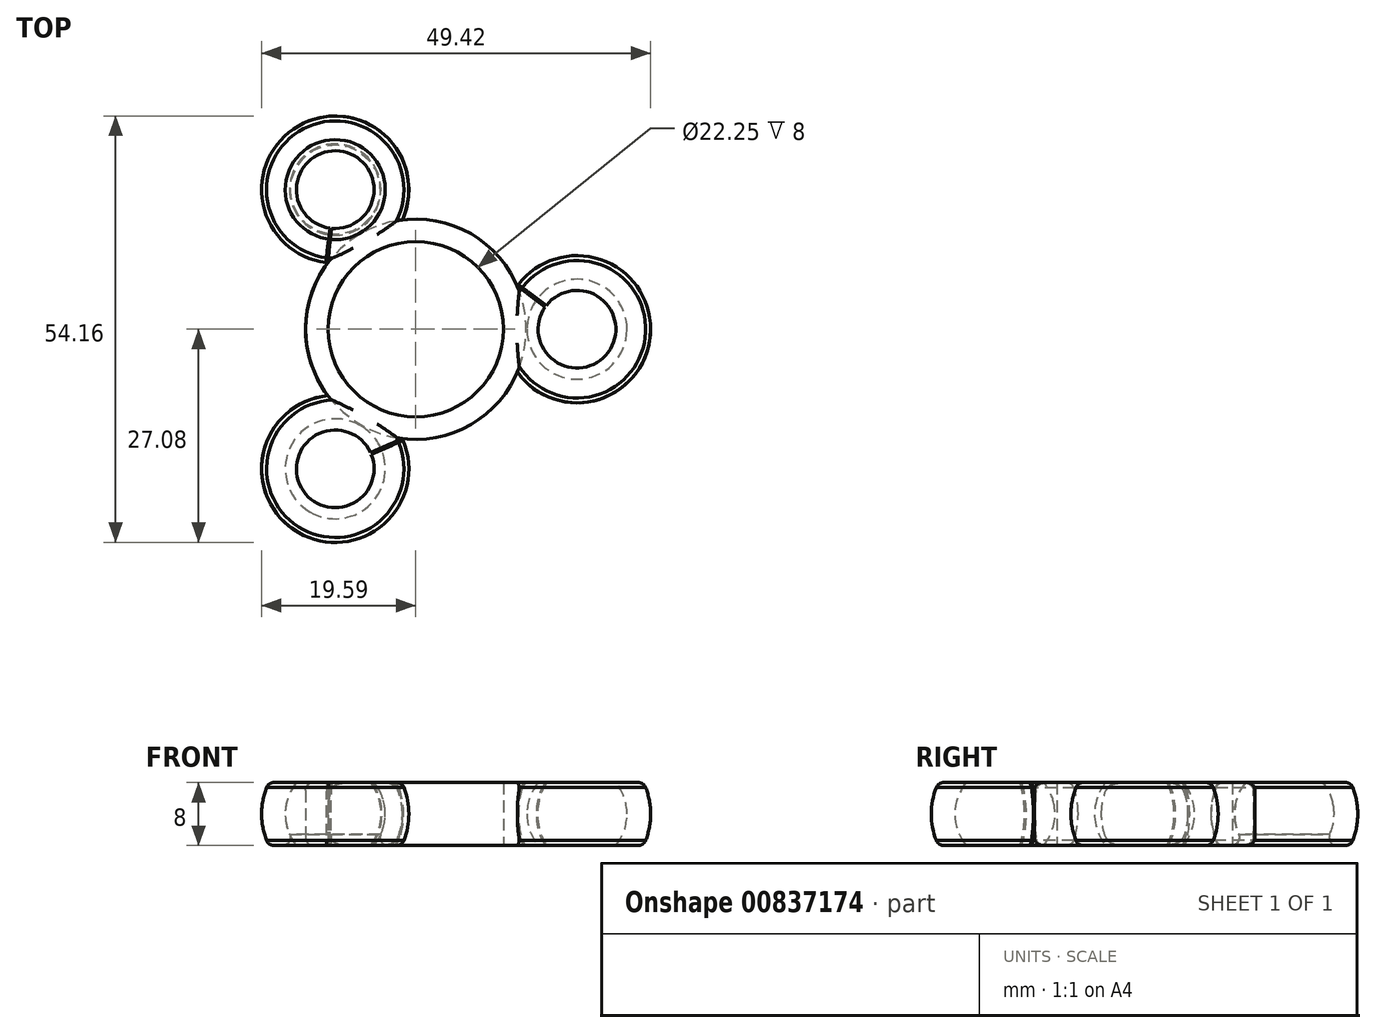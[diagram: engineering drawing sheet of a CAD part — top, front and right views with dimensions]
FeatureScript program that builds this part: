
annotation { "Feature Type Name" : "Feature", "Feature Type Description" : "" }
export const myFeature = defineFeature(function(context is Context, id is Id, definition is map)
    precondition{}
    {
        {
            var Q0;
            Q0=qCreatedBy(makeId("Top.planeOp"),FACE);
            var sketch = newSketch(context, id + "F0", { "sketchPlane" : qUnion([Q0])});
            skArc(sketch, "E0", {"start": v(29.82, 0) * mm, "mid": v(20.48, 9.35) * mm, "end": v(11.12, 0) * mm});
            skArc(sketch, "E1", {"start": v(26.83, 0) * mm, "mid": v(20.48, 6.35) * mm, "end": v(14.12, 0) * mm});
            skPoint(sketch, "E2.center", {"position": v(0, 0) * mm});
            skPoint(sketch, "E3", {"position": v(11.12, 0) * mm});
            skLineSegment(sketch, "E4", {"start": v(20.48, 0) * mm, "end": v(12.96, 5.57) * mm, "construction": true});
            skLineSegment(sketch, "E5", {"start": v(12.89, 5.47) * mm, "end": v(20.27, 0) * mm});
            skLineSegment(sketch, "E6", {"start": v(13.04, 5.67) * mm, "end": v(20.68, 0) * mm});
            skLineSegment(sketch, "E7", {"start": v(16.58, 2.73) * mm, "end": v(16.73, 2.93) * mm, "construction": true});
            skPoint(sketch, "E8", {"position": v(16.65, 2.83) * mm});
            skLineSegment(sketch, "E9", {"start": v(11.12, 0) * mm, "end": v(29.82, 0) * mm});
            skCircle(sketch, "E10.converted", {"center": v(0, 0) * mm, "radius": 14 * mm});
            skCircle(sketch, "E11.converted", {"center": v(0, 0) * mm, "radius": 11.12 * mm});
            skSolve(sketch);
        }
        {
            var Q0;
            {var subQ0=sQuery(id+"F0.wireOp",EDGE,"E9");var subQ1=sQuery(id+"F0.wireOp",EDGE,"E0");var subQ2=makeQuery(id+"F0.imprint","INTERSECT",VERTEX,{"derivedFrom":[subQ1,subQ0]});Q0=makeQuery(id+"F0.imprint","IMPRINT",FACE,{"disambiguationData":[TD([[makeQuery(id+"F0.imprint","IMPRINT",EDGE,{"disambiguationData":[TD([[subQ2,-1.0]])],"derivedFrom":subQ1}),1.0]])]});}
            var Q1;
            {var subQ0=sQuery(id+"F0.wireOp",EDGE,"E9");var subQ1=sQuery(id+"F0.wireOp",EDGE,"E0");var subQ2=makeQuery(id+"F0.imprint","INTERSECT",VERTEX,{"derivedFrom":[sQuery(id+"F0.wireOp",EDGE,"cSuj2Qlp-0pDQ-TG8P-6tV9-5ENMxgLf1ts3"),subQ1,subQ0]});Q1=makeQuery(id+"F0.imprint","IMPRINT",FACE,{"disambiguationData":[TD([[makeQuery(id+"F0.imprint","IMPRINT",EDGE,{"disambiguationData":[TD([[subQ2,1.0]])],"derivedFrom":subQ1}),1.0]])]});}
            var Q2;
            {var subQ1=sQuery(id+"F0.wireOp",EDGE,"E1");var subQ3=sQuery(id+"F0.wireOp",EDGE,"E5");var subQ4=makeQuery(id+"F0.imprint","INTERSECT",VERTEX,{"derivedFrom":[subQ1,subQ3]});Q2=makeQuery(id+"F0.imprint","IMPRINT",FACE,{"disambiguationData":[TD([[makeQuery(id+"F0.imprint","IMPRINT",EDGE,{"disambiguationData":[TD([[subQ4,-1.0]])],"derivedFrom":subQ1}),-1.0]])]});}
            var Q3;
            {var subQ3=sQuery(id+"F0.wireOp",EDGE,"E6");var subQ5=sQuery(id+"F0.wireOp",EDGE,"E1");var subQ7=makeQuery(id+"F0.imprint","INTERSECT",VERTEX,{"derivedFrom":[subQ5,subQ3]});Q3=makeQuery(id+"F0.imprint","IMPRINT",FACE,{"disambiguationData":[TD([[makeQuery(id+"F0.imprint","IMPRINT",EDGE,{"disambiguationData":[TD([[subQ7,-1.0]])],"derivedFrom":subQ5}),-1.0]])]});}
            var Q4;
            {var subQ0=sQuery(id+"F0.wireOp",EDGE,"E9");var subQ3=sQuery(id+"F0.wireOp",EDGE,"E10.converted");var subQ5=makeQuery(id+"F0.imprint","INTERSECT",VERTEX,{"derivedFrom":[subQ0,subQ3]});Q4=makeQuery(id+"F0.imprint","IMPRINT",FACE,{"disambiguationData":[TD([[makeQuery(id+"F0.imprint","IMPRINT",EDGE,{"disambiguationData":[TD([[subQ5,1.0]])],"derivedFrom":subQ0}),1.0]])]});}
            var Q5;
            Q5=sQuery(id+"F0.wireOp",EDGE,"E9");
            revolve(context, id + "F1", {"surfaceOperationType" : NewSurfaceOperationType.NEW, "entities" : qUnion([Q0, Q1, Q2, Q3, Q4]), "axis" : qUnion([Q5]), "revolveType" : RevolveType.FULL});
        }
        {
            var Q0;
            {var subQ0=sQuery(id+"F0.wireOp",EDGE,"E11.converted");Q0=makeQuery(id+"F0.imprint","IMPRINT",FACE,{"disambiguationData":[TD([[makeQuery(id+"F0.imprint","IMPRINT",EDGE,{"derivedFrom":subQ0}),-1.0]])]});}
            var Q1;
            {var subQ0=sQuery(id+"F0.wireOp",EDGE,"E9");var subQ3=sQuery(id+"F0.wireOp",EDGE,"E10.converted");var subQ5=makeQuery(id+"F0.imprint","INTERSECT",VERTEX,{"derivedFrom":[subQ0,subQ3]});Q1=makeQuery(id+"F0.imprint","IMPRINT",FACE,{"disambiguationData":[TD([[makeQuery(id+"F0.imprint","IMPRINT",EDGE,{"disambiguationData":[TD([[subQ5,1.0]])],"derivedFrom":subQ0}),1.0]])]});}
            extrude(context, id + "F2", {"entities" : qUnion([Q0, Q1]), "endBound" : BoundingType.SYMMETRIC, "depth" : 8 * mm, "offsetDistance" : 25 * mm});
        }
        {
            var Q0;
            {var subQ3=sQuery(id+"F0.wireOp",EDGE,"E6");var subQ5=sQuery(id+"F0.wireOp",EDGE,"E1");var subQ7=makeQuery(id+"F0.imprint","INTERSECT",VERTEX,{"derivedFrom":[subQ5,subQ3]});Q0=makeQuery(id+"F0.imprint","IMPRINT",FACE,{"disambiguationData":[TD([[makeQuery(id+"F0.imprint","IMPRINT",EDGE,{"disambiguationData":[TD([[subQ7,-1.0]])],"derivedFrom":subQ5}),-1.0]])]});}
            var Q1;
            {var subQ0=sQuery(id+"F0.wireOp",EDGE,"E6");var subQ1=sQuery(id+"F0.wireOp",EDGE,"E1");var subQ2=makeQuery(id+"F0.imprint","INTERSECT",VERTEX,{"derivedFrom":[subQ1,subQ0]});Q1=makeQuery(id+"F0.imprint","IMPRINT",FACE,{"disambiguationData":[TD([[makeQuery(id+"F0.imprint","IMPRINT",EDGE,{"disambiguationData":[TD([[subQ2,-1.0]])],"derivedFrom":subQ1}),1.0]])]});}
            extrude(context, id + "F3", {"entities" : qUnion([Q0, Q1]), "operationType" : NewBodyOperationType.REMOVE, "endBound" : BoundingType.SYMMETRIC, "oppositeDirection" : true, "depth" : 25 * mm, "offsetDistance" : 25 * mm});
        }
        {
            var Q0;
            Q0=makeQuery(id+"F2.opExtrude","CAP_FACE",FACE,{"disambiguationData":[OSD([sQuery(id+"F0.wireOp",EDGE,"E10.converted"),sQuery(id+"F0.wireOp",EDGE,"E11.converted")])],"isStart":false});
            var sketch = newSketch(context, id + "F4", { "sketchPlane" : qUnion([Q0])});
            skCircle(sketch, "E12", {"center": v(20.48, 0) * mm, "radius": 9.35 * mm});
            skSolve(sketch);
        }
        {
            var Q0;
            {var subQ0=sQuery(id+"F4.wireOp",EDGE,"E12");var subQ1=makeQuery(id+"F2.opExtrude","CAP_EDGE",EDGE,{"disambiguationData":[OSD([sQuery(id+"F0.wireOp",EDGE,"EpLUkTgh-srj3-UDcm-vpLL-Aj0M4960BcQC")])],"isStart":false});var subQ2=makeQuery(id+"F4.imprint","INTERSECT",VERTEX,{"disambiguationData":[OD(0.0)],"derivedFrom":[subQ1,subQ0]});Q0=makeQuery(id+"F4.imprint","IMPRINT",FACE,{"disambiguationData":[TD([[makeQuery(id+"F4.imprint","IMPRINT",EDGE,{"disambiguationData":[TD([[subQ2,1.0]])],"derivedFrom":subQ0}),1.0]])]});}
            var Q1;
            {var subQ0=sQuery(id+"F4.wireOp",EDGE,"E12");var subQ1=makeQuery(id+"F4.imprint","INTERSECT",VERTEX,{"derivedFrom":[makeQuery(id+"F2.opExtrude","CAP_EDGE",EDGE,{"disambiguationData":[OSD([sQuery(id+"F0.wireOp",EDGE,"cSuj2Qlp-0pDQ-TG8P-6tV9-5ENMxgLf1ts3")])],"isStart":false}),subQ0]});Q1=makeQuery(id+"F4.imprint","IMPRINT",FACE,{"disambiguationData":[TD([[makeQuery(id+"F4.imprint","IMPRINT",EDGE,{"disambiguationData":[TD([[subQ1,1.0]])],"derivedFrom":subQ0}),1.0]])]});}
            extrude(context, id + "F5", {"entities" : qUnion([Q0, Q1]), "endBound" : BoundingType.THROUGH_ALL, "depth" : 25 * mm, "offsetDistance" : 25 * mm});
        }
        {
            var Q0;
            Q0=makeQuery(id+"F5.opExtrude","SWEPT_BODY",BODY,{"disambiguationData":[OSD([sQuery(id+"F4.wireOp",EDGE,"E12")])]});
            var Q1;
            Q1=qCreatedBy(makeId("Top.planeOp"),FACE);
            mirror(context, id + "F6", {"entities" : qUnion([Q0]), "mirrorPlane" : qUnion([Q1])});
        }
        {
            var Q0;
            Q0=makeQuery(id+"F5.opExtrude","SWEPT_BODY",BODY,{"disambiguationData":[OSD([sQuery(id+"F4.wireOp",EDGE,"E12")])]});
            var Q1;
            Q1=makeQuery(id+"F6.opPattern","COPY",BODY,{"derivedFrom":makeQuery(id+"F5.opExtrude","SWEPT_BODY",BODY,{"disambiguationData":[OSD([sQuery(id+"F4.wireOp",EDGE,"E12")])]}),"instanceName":"1"});
            var Q2;
            Q2=makeQuery(id+"F2.opExtrude","SWEPT_BODY",BODY,{"disambiguationData":[OSD([sQuery(id+"F0.wireOp",EDGE,"cSuj2Qlp-0pDQ-TG8P-6tV9-5ENMxgLf1ts3"),sQuery(id+"F0.wireOp",EDGE,"EpLUkTgh-srj3-UDcm-vpLL-Aj0M4960BcQC"),sQuery(id+"F0.wireOp",EDGE,"zkzayk11-GNPU-wToI-XGPR-Ek0oZkHYU3Nr"),sQuery(id+"F0.wireOp",EDGE,"hWNBNIeG-xdyR-n3hM-UmGh-ZOXQKCDM2jcM")])]});
            var Q3;
            Q3=makeQuery(id+"F1.opRevolve","SWEPT_BODY",BODY,{"disambiguationData":[OSD([sQuery(id+"F0.wireOp",EDGE,"E0"),sQuery(id+"F0.wireOp",EDGE,"E1"),sQuery(id+"F0.wireOp",EDGE,"E9")])]});
            booleanBodies(context, id + "F7", {"operationType" : BooleanOperationType.SUBTRACTION, "tools" : qUnion([Q0, Q1]), "targets" : qUnion([Q2, Q3])});
        }
        {
            var Q0;
            Q0=qCreatedBy(makeId("Front.planeOp"),FACE);
            var sketch = newSketch(context, id + "F8", { "sketchPlane" : qUnion([Q0])});
            skLineSegment(sketch, "E13", {"start": v(0, 0) * mm, "end": v(0, 13.43) * mm, "construction": true});
            skSolve(sketch);
        }
        {
            var Q0;
            Q0=makeQuery(id+"F1.opRevolve","SWEPT_BODY",BODY,{"disambiguationData":[OSD([sQuery(id+"F0.wireOp",EDGE,"E0"),sQuery(id+"F0.wireOp",EDGE,"E1"),sQuery(id+"F0.wireOp",EDGE,"E9")])]});
            var Q1;
            Q1=sQuery(id+"F8.wireOp",EDGE,"E13");
            circularPattern(context, id + "F9", {"entities" : qUnion([Q0]), "axis" : qUnion([Q1]), "angle" : 360 * degree, "instanceCount" : 3, "equalSpace" : true});
        }
        {
            var Q0;
            Q0=makeQuery(id+"F1.opRevolve","SWEPT_BODY",BODY,{"disambiguationData":[OSD([sQuery(id+"F0.wireOp",EDGE,"E0"),sQuery(id+"F0.wireOp",EDGE,"E1"),sQuery(id+"F0.wireOp",EDGE,"E9")])]});
            var Q1;
            Q1=makeQuery(id+"F2.opExtrude","SWEPT_BODY",BODY,{"disambiguationData":[OSD([sQuery(id+"F0.wireOp",EDGE,"cSuj2Qlp-0pDQ-TG8P-6tV9-5ENMxgLf1ts3"),sQuery(id+"F0.wireOp",EDGE,"EpLUkTgh-srj3-UDcm-vpLL-Aj0M4960BcQC"),sQuery(id+"F0.wireOp",EDGE,"zkzayk11-GNPU-wToI-XGPR-Ek0oZkHYU3Nr"),sQuery(id+"F0.wireOp",EDGE,"hWNBNIeG-xdyR-n3hM-UmGh-ZOXQKCDM2jcM")])]});
            var Q2;
            Q2=makeQuery(id+"F9.opPattern","COPY",BODY,{"derivedFrom":makeQuery(id+"F1.opRevolve","SWEPT_BODY",BODY,{"disambiguationData":[OSD([sQuery(id+"F0.wireOp",EDGE,"E0"),sQuery(id+"F0.wireOp",EDGE,"E1"),sQuery(id+"F0.wireOp",EDGE,"E9")])]}),"instanceName":"1"});
            var Q3;
            Q3=makeQuery(id+"F9.opPattern","COPY",BODY,{"derivedFrom":makeQuery(id+"F1.opRevolve","SWEPT_BODY",BODY,{"disambiguationData":[OSD([sQuery(id+"F0.wireOp",EDGE,"E0"),sQuery(id+"F0.wireOp",EDGE,"E1"),sQuery(id+"F0.wireOp",EDGE,"E9")])]}),"instanceName":"2"});
            var Q4;
            Q4=makeQuery(id+"F2.opExtrude","SWEPT_BODY",BODY,{"disambiguationData":[OSD([sQuery(id+"F0.wireOp",EDGE,"E10.converted"),sQuery(id+"F0.wireOp",EDGE,"E11.converted")])]});
            booleanBodies(context, id + "F10", {"operationType" : BooleanOperationType.UNION, "tools" : qUnion([Q0, Q1, Q2, Q3, Q4])});
        }
        {
            var Q0;
            {var subQ0=makeQuery(id+"F7.opBoolean","COPY",FACE,{"derivedFrom":makeQuery(id+"F5.opExtrude","CAP_FACE",FACE,{"disambiguationData":[OSD([sQuery(id+"F4.wireOp",EDGE,"E12")])],"isStart":true})});var subQ1=sQuery(id+"F0.wireOp",EDGE,"E10.converted");var subQ2=makeQuery(id+"F1.opRevolve","SWEPT_FACE",FACE,{"disambiguationData":[OSD([sQuery(id+"F0.wireOp",EDGE,"E0")])]});Q0=makeQuery(id+"F10.opBoolean","SPLIT",EDGE,{"disambiguationData":[TD([makeQuery(id+"F2.opExtrude","SWEPT_FACE",FACE,{"disambiguationData":[OSD([subQ1])]}),makeQuery(id+"F2.opExtrude","CAP_FACE",FACE,{"disambiguationData":[OSD([subQ1,sQuery(id+"F0.wireOp",EDGE,"E11.converted")])],"isStart":false}),subQ0,makeQuery(id+"F9.opPattern","COPY",FACE,{"derivedFrom":subQ0,"instanceName":"1"}),makeQuery(id+"F9.opPattern","COPY",FACE,{"derivedFrom":subQ2,"instanceName":"1"}),makeQuery(id+"F9.opPattern","COPY",FACE,{"derivedFrom":subQ0,"instanceName":"2"}),makeQuery(id+"F9.opPattern","COPY",FACE,{"derivedFrom":subQ2,"instanceName":"2"})])],"derivedFrom":makeQuery(id+"F2.opExtrude","CAP_EDGE",EDGE,{"disambiguationData":[OSD([subQ1])],"isStart":false})});}
            var Q1;
            {var subQ0=makeQuery(id+"F5.opExtrude","CAP_FACE",FACE,{"disambiguationData":[OSD([sQuery(id+"F4.wireOp",EDGE,"E12")])],"isStart":true});var subQ3=makeQuery(id+"F1.opRevolve","SWEPT_FACE",FACE,{"disambiguationData":[OSD([sQuery(id+"F0.wireOp",EDGE,"E0")])]});Q1=makeQuery(id+"F10.opBoolean","SPLIT",EDGE,{"disambiguationData":[TD([makeQuery(id+"F9.opPattern","COPY",FACE,{"derivedFrom":makeQuery(id+"F3.boolean.opBoolean","COPY",FACE,{"derivedFrom":makeQuery(id+"F3.opExtrude","SWEPT_FACE",FACE,{"disambiguationData":[OSD([sQuery(id+"F0.wireOp",EDGE,"E6")])]})}),"instanceName":"2"})])],"derivedFrom":makeQuery(id+"F9.opPattern","COPY",EDGE,{"derivedFrom":makeQuery(id+"F7.opBoolean","INTERSECT",EDGE,{"derivedFrom":[subQ3,subQ0]}),"instanceName":"2"})});}
            var Q2;
            {var subQ0=makeQuery(id+"F7.opBoolean","COPY",FACE,{"derivedFrom":makeQuery(id+"F5.opExtrude","CAP_FACE",FACE,{"disambiguationData":[OSD([sQuery(id+"F4.wireOp",EDGE,"E12")])],"isStart":true})});var subQ1=sQuery(id+"F0.wireOp",EDGE,"E10.converted");var subQ2=makeQuery(id+"F1.opRevolve","SWEPT_FACE",FACE,{"disambiguationData":[OSD([sQuery(id+"F0.wireOp",EDGE,"E0")])]});Q2=makeQuery(id+"F10.opBoolean","SPLIT",EDGE,{"disambiguationData":[TD([subQ2,makeQuery(id+"F2.opExtrude","SWEPT_FACE",FACE,{"disambiguationData":[OSD([subQ1])]}),makeQuery(id+"F2.opExtrude","CAP_FACE",FACE,{"disambiguationData":[OSD([subQ1,sQuery(id+"F0.wireOp",EDGE,"E11.converted")])],"isStart":false}),subQ0,makeQuery(id+"F9.opPattern","COPY",FACE,{"derivedFrom":subQ0,"instanceName":"1"}),makeQuery(id+"F9.opPattern","COPY",FACE,{"derivedFrom":subQ0,"instanceName":"2"}),makeQuery(id+"F9.opPattern","COPY",FACE,{"derivedFrom":subQ2,"instanceName":"2"})])],"derivedFrom":makeQuery(id+"F2.opExtrude","CAP_EDGE",EDGE,{"disambiguationData":[OSD([subQ1])],"isStart":false})});}
            var Q3;
            {var subQ1=makeQuery(id+"F5.opExtrude","CAP_FACE",FACE,{"disambiguationData":[OSD([sQuery(id+"F4.wireOp",EDGE,"E12")])],"isStart":true});var subQ3=makeQuery(id+"F1.opRevolve","SWEPT_FACE",FACE,{"disambiguationData":[OSD([sQuery(id+"F0.wireOp",EDGE,"E0")])]});Q3=makeQuery(id+"F10.opBoolean","SPLIT",EDGE,{"disambiguationData":[TD([makeQuery(id+"F3.boolean.opBoolean","COPY",FACE,{"derivedFrom":makeQuery(id+"F3.opExtrude","SWEPT_FACE",FACE,{"disambiguationData":[OSD([sQuery(id+"F0.wireOp",EDGE,"E6")])]})})])],"derivedFrom":makeQuery(id+"F7.opBoolean","INTERSECT",EDGE,{"derivedFrom":[subQ3,subQ1]})});}
            var Q4;
            {var subQ0=makeQuery(id+"F5.opExtrude","CAP_FACE",FACE,{"disambiguationData":[OSD([sQuery(id+"F4.wireOp",EDGE,"E12")])],"isStart":true});var subQ3=makeQuery(id+"F1.opRevolve","SWEPT_FACE",FACE,{"disambiguationData":[OSD([sQuery(id+"F0.wireOp",EDGE,"E0")])]});Q4=makeQuery(id+"F10.opBoolean","SPLIT",EDGE,{"disambiguationData":[TD([makeQuery(id+"F9.opPattern","COPY",FACE,{"derivedFrom":makeQuery(id+"F3.boolean.opBoolean","COPY",FACE,{"derivedFrom":makeQuery(id+"F3.opExtrude","SWEPT_FACE",FACE,{"disambiguationData":[OSD([sQuery(id+"F0.wireOp",EDGE,"E6")])]})}),"instanceName":"1"})])],"derivedFrom":makeQuery(id+"F9.opPattern","COPY",EDGE,{"derivedFrom":makeQuery(id+"F7.opBoolean","INTERSECT",EDGE,{"derivedFrom":[subQ3,subQ0]}),"instanceName":"1"})});}
            var Q5;
            {var subQ1=makeQuery(id+"F6.opPattern","COPY",FACE,{"derivedFrom":makeQuery(id+"F5.opExtrude","CAP_FACE",FACE,{"disambiguationData":[OSD([sQuery(id+"F4.wireOp",EDGE,"E12")])],"isStart":true}),"instanceName":"1"});var subQ3=makeQuery(id+"F1.opRevolve","SWEPT_FACE",FACE,{"disambiguationData":[OSD([sQuery(id+"F0.wireOp",EDGE,"E0")])]});Q5=makeQuery(id+"F10.opBoolean","SPLIT",EDGE,{"disambiguationData":[TD([makeQuery(id+"F3.boolean.opBoolean","COPY",FACE,{"derivedFrom":makeQuery(id+"F3.opExtrude","SWEPT_FACE",FACE,{"disambiguationData":[OSD([sQuery(id+"F0.wireOp",EDGE,"E6")])]})})])],"derivedFrom":makeQuery(id+"F7.opBoolean","INTERSECT",EDGE,{"derivedFrom":[subQ3,subQ1]})});}
            var Q6;
            {var subQ0=sQuery(id+"F0.wireOp",EDGE,"E10.converted");var subQ1=makeQuery(id+"F7.opBoolean","COPY",FACE,{"derivedFrom":makeQuery(id+"F6.opPattern","COPY",FACE,{"derivedFrom":makeQuery(id+"F5.opExtrude","CAP_FACE",FACE,{"disambiguationData":[OSD([sQuery(id+"F4.wireOp",EDGE,"E12")])],"isStart":true}),"instanceName":"1"})});var subQ2=makeQuery(id+"F1.opRevolve","SWEPT_FACE",FACE,{"disambiguationData":[OSD([sQuery(id+"F0.wireOp",EDGE,"E0")])]});Q6=makeQuery(id+"F10.opBoolean","SPLIT",EDGE,{"disambiguationData":[TD([subQ2,makeQuery(id+"F2.opExtrude","SWEPT_FACE",FACE,{"disambiguationData":[OSD([subQ0])]}),makeQuery(id+"F2.opExtrude","CAP_FACE",FACE,{"disambiguationData":[OSD([subQ0,sQuery(id+"F0.wireOp",EDGE,"E11.converted")])],"isStart":true}),subQ1,makeQuery(id+"F9.opPattern","COPY",FACE,{"derivedFrom":subQ1,"instanceName":"1"}),makeQuery(id+"F9.opPattern","COPY",FACE,{"derivedFrom":subQ1,"instanceName":"2"}),makeQuery(id+"F9.opPattern","COPY",FACE,{"derivedFrom":subQ2,"instanceName":"2"})])],"derivedFrom":makeQuery(id+"F2.opExtrude","CAP_EDGE",EDGE,{"disambiguationData":[OSD([subQ0])],"isStart":true})});}
            var Q7;
            {var subQ0=makeQuery(id+"F6.opPattern","COPY",FACE,{"derivedFrom":makeQuery(id+"F5.opExtrude","CAP_FACE",FACE,{"disambiguationData":[OSD([sQuery(id+"F4.wireOp",EDGE,"E12")])],"isStart":true}),"instanceName":"1"});var subQ3=makeQuery(id+"F1.opRevolve","SWEPT_FACE",FACE,{"disambiguationData":[OSD([sQuery(id+"F0.wireOp",EDGE,"E0")])]});Q7=makeQuery(id+"F10.opBoolean","SPLIT",EDGE,{"disambiguationData":[TD([makeQuery(id+"F9.opPattern","COPY",FACE,{"derivedFrom":makeQuery(id+"F3.boolean.opBoolean","COPY",FACE,{"derivedFrom":makeQuery(id+"F3.opExtrude","SWEPT_FACE",FACE,{"disambiguationData":[OSD([sQuery(id+"F0.wireOp",EDGE,"E6")])]})}),"instanceName":"2"})])],"derivedFrom":makeQuery(id+"F9.opPattern","COPY",EDGE,{"derivedFrom":makeQuery(id+"F7.opBoolean","INTERSECT",EDGE,{"derivedFrom":[subQ3,subQ0]}),"instanceName":"2"})});}
            var Q8;
            {var subQ0=makeQuery(id+"F7.opBoolean","COPY",FACE,{"derivedFrom":makeQuery(id+"F6.opPattern","COPY",FACE,{"derivedFrom":makeQuery(id+"F5.opExtrude","CAP_FACE",FACE,{"disambiguationData":[OSD([sQuery(id+"F4.wireOp",EDGE,"E12")])],"isStart":true}),"instanceName":"1"})});var subQ1=sQuery(id+"F0.wireOp",EDGE,"E10.converted");var subQ2=makeQuery(id+"F1.opRevolve","SWEPT_FACE",FACE,{"disambiguationData":[OSD([sQuery(id+"F0.wireOp",EDGE,"E0")])]});Q8=makeQuery(id+"F10.opBoolean","SPLIT",EDGE,{"disambiguationData":[TD([makeQuery(id+"F2.opExtrude","SWEPT_FACE",FACE,{"disambiguationData":[OSD([subQ1])]}),makeQuery(id+"F2.opExtrude","CAP_FACE",FACE,{"disambiguationData":[OSD([subQ1,sQuery(id+"F0.wireOp",EDGE,"E11.converted")])],"isStart":true}),subQ0,makeQuery(id+"F9.opPattern","COPY",FACE,{"derivedFrom":subQ0,"instanceName":"1"}),makeQuery(id+"F9.opPattern","COPY",FACE,{"derivedFrom":subQ2,"instanceName":"1"}),makeQuery(id+"F9.opPattern","COPY",FACE,{"derivedFrom":subQ0,"instanceName":"2"}),makeQuery(id+"F9.opPattern","COPY",FACE,{"derivedFrom":subQ2,"instanceName":"2"})])],"derivedFrom":makeQuery(id+"F2.opExtrude","CAP_EDGE",EDGE,{"disambiguationData":[OSD([subQ1])],"isStart":true})});}
            var Q9;
            {var subQ0=makeQuery(id+"F6.opPattern","COPY",FACE,{"derivedFrom":makeQuery(id+"F5.opExtrude","CAP_FACE",FACE,{"disambiguationData":[OSD([sQuery(id+"F4.wireOp",EDGE,"E12")])],"isStart":true}),"instanceName":"1"});var subQ3=makeQuery(id+"F1.opRevolve","SWEPT_FACE",FACE,{"disambiguationData":[OSD([sQuery(id+"F0.wireOp",EDGE,"E0")])]});Q9=makeQuery(id+"F10.opBoolean","SPLIT",EDGE,{"disambiguationData":[TD([makeQuery(id+"F9.opPattern","COPY",FACE,{"derivedFrom":makeQuery(id+"F3.boolean.opBoolean","COPY",FACE,{"derivedFrom":makeQuery(id+"F3.opExtrude","SWEPT_FACE",FACE,{"disambiguationData":[OSD([sQuery(id+"F0.wireOp",EDGE,"E6")])]})}),"instanceName":"1"})])],"derivedFrom":makeQuery(id+"F9.opPattern","COPY",EDGE,{"derivedFrom":makeQuery(id+"F7.opBoolean","INTERSECT",EDGE,{"derivedFrom":[subQ3,subQ0]}),"instanceName":"1"})});}
            var Q10;
            {var subQ0=sQuery(id+"F0.wireOp",EDGE,"E10.converted");var subQ1=makeQuery(id+"F7.opBoolean","COPY",FACE,{"derivedFrom":makeQuery(id+"F6.opPattern","COPY",FACE,{"derivedFrom":makeQuery(id+"F5.opExtrude","CAP_FACE",FACE,{"disambiguationData":[OSD([sQuery(id+"F4.wireOp",EDGE,"E12")])],"isStart":true}),"instanceName":"1"})});var subQ2=makeQuery(id+"F1.opRevolve","SWEPT_FACE",FACE,{"disambiguationData":[OSD([sQuery(id+"F0.wireOp",EDGE,"E0")])]});Q10=makeQuery(id+"F10.opBoolean","SPLIT",EDGE,{"disambiguationData":[TD([subQ2,makeQuery(id+"F2.opExtrude","SWEPT_FACE",FACE,{"disambiguationData":[OSD([subQ0])]}),makeQuery(id+"F2.opExtrude","CAP_FACE",FACE,{"disambiguationData":[OSD([subQ0,sQuery(id+"F0.wireOp",EDGE,"E11.converted")])],"isStart":true}),subQ1,makeQuery(id+"F9.opPattern","COPY",FACE,{"derivedFrom":subQ1,"instanceName":"1"}),makeQuery(id+"F9.opPattern","COPY",FACE,{"derivedFrom":subQ2,"instanceName":"1"}),makeQuery(id+"F9.opPattern","COPY",FACE,{"derivedFrom":subQ1,"instanceName":"2"})])],"derivedFrom":makeQuery(id+"F2.opExtrude","CAP_EDGE",EDGE,{"disambiguationData":[OSD([subQ0])],"isStart":true})});}
            var Q11;
            {var subQ0=makeQuery(id+"F7.opBoolean","COPY",FACE,{"derivedFrom":makeQuery(id+"F5.opExtrude","CAP_FACE",FACE,{"disambiguationData":[OSD([sQuery(id+"F4.wireOp",EDGE,"E12")])],"isStart":true})});var subQ1=sQuery(id+"F0.wireOp",EDGE,"E10.converted");var subQ2=makeQuery(id+"F1.opRevolve","SWEPT_FACE",FACE,{"disambiguationData":[OSD([sQuery(id+"F0.wireOp",EDGE,"E0")])]});Q11=makeQuery(id+"F10.opBoolean","SPLIT",EDGE,{"disambiguationData":[TD([subQ2,makeQuery(id+"F2.opExtrude","SWEPT_FACE",FACE,{"disambiguationData":[OSD([subQ1])]}),makeQuery(id+"F2.opExtrude","CAP_FACE",FACE,{"disambiguationData":[OSD([subQ1,sQuery(id+"F0.wireOp",EDGE,"E11.converted")])],"isStart":false}),subQ0,makeQuery(id+"F9.opPattern","COPY",FACE,{"derivedFrom":subQ0,"instanceName":"1"}),makeQuery(id+"F9.opPattern","COPY",FACE,{"derivedFrom":subQ2,"instanceName":"1"}),makeQuery(id+"F9.opPattern","COPY",FACE,{"derivedFrom":subQ0,"instanceName":"2"})])],"derivedFrom":makeQuery(id+"F2.opExtrude","CAP_EDGE",EDGE,{"disambiguationData":[OSD([subQ1])],"isStart":false})});}
            var Q12;
            {var subQ1=makeQuery(id+"F5.opExtrude","CAP_FACE",FACE,{"disambiguationData":[OSD([sQuery(id+"F4.wireOp",EDGE,"E12")])],"isStart":true});var subQ3=makeQuery(id+"F1.opRevolve","SWEPT_FACE",FACE,{"disambiguationData":[OSD([sQuery(id+"F0.wireOp",EDGE,"E0")])]});Q12=makeQuery(id+"F10.opBoolean","SPLIT",EDGE,{"disambiguationData":[TD([makeQuery(id+"F3.boolean.opBoolean","COPY",FACE,{"derivedFrom":makeQuery(id+"F3.opExtrude","SWEPT_FACE",FACE,{"disambiguationData":[OSD([sQuery(id+"F0.wireOp",EDGE,"E5")])]})})])],"derivedFrom":makeQuery(id+"F7.opBoolean","INTERSECT",EDGE,{"derivedFrom":[subQ3,subQ1]})});}
            var Q13;
            {var subQ0=makeQuery(id+"F6.opPattern","COPY",FACE,{"derivedFrom":makeQuery(id+"F5.opExtrude","CAP_FACE",FACE,{"disambiguationData":[OSD([sQuery(id+"F4.wireOp",EDGE,"E12")])],"isStart":true}),"instanceName":"1"});var subQ3=makeQuery(id+"F1.opRevolve","SWEPT_FACE",FACE,{"disambiguationData":[OSD([sQuery(id+"F0.wireOp",EDGE,"E0")])]});Q13=makeQuery(id+"F10.opBoolean","SPLIT",EDGE,{"disambiguationData":[TD([makeQuery(id+"F3.boolean.opBoolean","COPY",FACE,{"derivedFrom":makeQuery(id+"F3.opExtrude","SWEPT_FACE",FACE,{"disambiguationData":[OSD([sQuery(id+"F0.wireOp",EDGE,"E5")])]})})])],"derivedFrom":makeQuery(id+"F7.opBoolean","INTERSECT",EDGE,{"derivedFrom":[subQ3,subQ0]})});}
            var Q14;
            {var subQ0=makeQuery(id+"F5.opExtrude","CAP_FACE",FACE,{"disambiguationData":[OSD([sQuery(id+"F4.wireOp",EDGE,"E12")])],"isStart":true});var subQ3=makeQuery(id+"F1.opRevolve","SWEPT_FACE",FACE,{"disambiguationData":[OSD([sQuery(id+"F0.wireOp",EDGE,"E0")])]});Q14=makeQuery(id+"F10.opBoolean","SPLIT",EDGE,{"disambiguationData":[TD([makeQuery(id+"F9.opPattern","COPY",FACE,{"derivedFrom":makeQuery(id+"F3.boolean.opBoolean","COPY",FACE,{"derivedFrom":makeQuery(id+"F3.opExtrude","SWEPT_FACE",FACE,{"disambiguationData":[OSD([sQuery(id+"F0.wireOp",EDGE,"E5")])]})}),"instanceName":"2"})])],"derivedFrom":makeQuery(id+"F9.opPattern","COPY",EDGE,{"derivedFrom":makeQuery(id+"F7.opBoolean","INTERSECT",EDGE,{"derivedFrom":[subQ3,subQ0]}),"instanceName":"2"})});}
            var Q15;
            {var subQ0=makeQuery(id+"F6.opPattern","COPY",FACE,{"derivedFrom":makeQuery(id+"F5.opExtrude","CAP_FACE",FACE,{"disambiguationData":[OSD([sQuery(id+"F4.wireOp",EDGE,"E12")])],"isStart":true}),"instanceName":"1"});var subQ3=makeQuery(id+"F1.opRevolve","SWEPT_FACE",FACE,{"disambiguationData":[OSD([sQuery(id+"F0.wireOp",EDGE,"E0")])]});Q15=makeQuery(id+"F10.opBoolean","SPLIT",EDGE,{"disambiguationData":[TD([makeQuery(id+"F9.opPattern","COPY",FACE,{"derivedFrom":makeQuery(id+"F3.boolean.opBoolean","COPY",FACE,{"derivedFrom":makeQuery(id+"F3.opExtrude","SWEPT_FACE",FACE,{"disambiguationData":[OSD([sQuery(id+"F0.wireOp",EDGE,"E5")])]})}),"instanceName":"2"})])],"derivedFrom":makeQuery(id+"F9.opPattern","COPY",EDGE,{"derivedFrom":makeQuery(id+"F7.opBoolean","INTERSECT",EDGE,{"derivedFrom":[subQ3,subQ0]}),"instanceName":"2"})});}
            var Q16;
            Q16=makeQuery(id+"F9.opPattern","COPY",EDGE,{"derivedFrom":makeQuery(id+"F7.opBoolean","INTERSECT",EDGE,{"derivedFrom":[makeQuery(id+"F1.opRevolve","SWEPT_FACE",FACE,{"disambiguationData":[OSD([sQuery(id+"F0.wireOp",EDGE,"E1")])]}),makeQuery(id+"F6.opPattern","COPY",FACE,{"derivedFrom":makeQuery(id+"F5.opExtrude","CAP_FACE",FACE,{"disambiguationData":[OSD([sQuery(id+"F4.wireOp",EDGE,"E12")])],"isStart":true}),"instanceName":"1"})]}),"instanceName":"1"});
            var Q17;
            {var subQ0=makeQuery(id+"F6.opPattern","COPY",FACE,{"derivedFrom":makeQuery(id+"F5.opExtrude","CAP_FACE",FACE,{"disambiguationData":[OSD([sQuery(id+"F4.wireOp",EDGE,"E12")])],"isStart":true}),"instanceName":"1"});var subQ3=makeQuery(id+"F1.opRevolve","SWEPT_FACE",FACE,{"disambiguationData":[OSD([sQuery(id+"F0.wireOp",EDGE,"E0")])]});Q17=makeQuery(id+"F10.opBoolean","SPLIT",EDGE,{"disambiguationData":[TD([makeQuery(id+"F9.opPattern","COPY",FACE,{"derivedFrom":makeQuery(id+"F3.boolean.opBoolean","COPY",FACE,{"derivedFrom":makeQuery(id+"F3.opExtrude","SWEPT_FACE",FACE,{"disambiguationData":[OSD([sQuery(id+"F0.wireOp",EDGE,"E5")])]})}),"instanceName":"1"})])],"derivedFrom":makeQuery(id+"F9.opPattern","COPY",EDGE,{"derivedFrom":makeQuery(id+"F7.opBoolean","INTERSECT",EDGE,{"derivedFrom":[subQ3,subQ0]}),"instanceName":"1"})});}
            var Q18;
            {var subQ0=makeQuery(id+"F5.opExtrude","CAP_FACE",FACE,{"disambiguationData":[OSD([sQuery(id+"F4.wireOp",EDGE,"E12")])],"isStart":true});var subQ3=makeQuery(id+"F1.opRevolve","SWEPT_FACE",FACE,{"disambiguationData":[OSD([sQuery(id+"F0.wireOp",EDGE,"E0")])]});Q18=makeQuery(id+"F10.opBoolean","SPLIT",EDGE,{"disambiguationData":[TD([makeQuery(id+"F9.opPattern","COPY",FACE,{"derivedFrom":makeQuery(id+"F3.boolean.opBoolean","COPY",FACE,{"derivedFrom":makeQuery(id+"F3.opExtrude","SWEPT_FACE",FACE,{"disambiguationData":[OSD([sQuery(id+"F0.wireOp",EDGE,"E5")])]})}),"instanceName":"1"})])],"derivedFrom":makeQuery(id+"F9.opPattern","COPY",EDGE,{"derivedFrom":makeQuery(id+"F7.opBoolean","INTERSECT",EDGE,{"derivedFrom":[subQ3,subQ0]}),"instanceName":"1"})});}
            fillet(context, id + "F11", {"entities" : qUnion([Q0, Q1, Q2, Q3, Q4, Q5, Q6, Q7, Q8, Q9, Q10, Q11, Q12, Q13, Q14, Q15, Q16, Q17, Q18]), "radius" : 1 * mm, "tangentPropagation" : true, "allowEdgeOverflow" : false});
        }
    });
